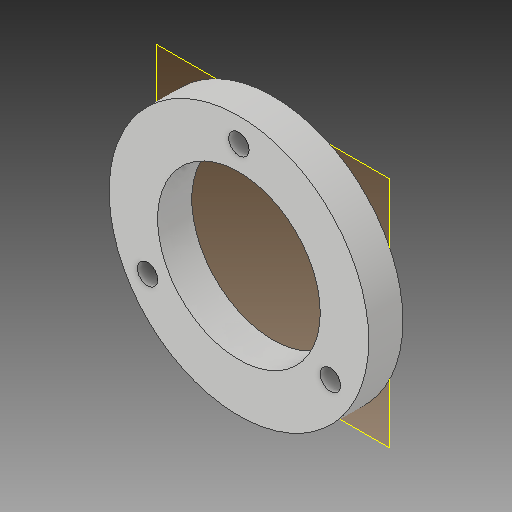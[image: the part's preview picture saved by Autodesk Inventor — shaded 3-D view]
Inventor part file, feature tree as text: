
AUTODESK INVENTOR PART (.ipt)
format: ipt  version: 2018.3 (Build 223284000, 284)  size: 109,568 bytes
history: native  units: mm
features: other x5, extrude x1, sketch x1
ambient origin geometry x8: Origin, YZ Plane, XZ Plane, XY Plane, X Axis, Y Axis, Z Axis, Center Point
bodies: Body1 (feature_tree)
feature tree (7):
  other  "Твердое тело1"
  other  "РабПлоскость1"
  extrude  "Выдавливание1"  Depth=5.0mm TaperAngle=0.0deg
  sketch  "Эскиз1"
  other  "<userpath>\GoogleDrive\My_project\Механика\Кофемашина\Inventor\Сборка.iam"
  other  "Сборка.iam"
  other  "Ось:1"
